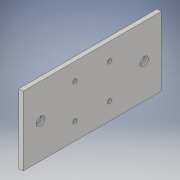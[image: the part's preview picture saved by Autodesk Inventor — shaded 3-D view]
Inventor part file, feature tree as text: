
AUTODESK INVENTOR PART (.ipt)
format: ipt  version: 2017 (Build 210142000, 142)  size: 106,496 bytes
history: native  units: in
note: dims shown in document units (in); Inventor stores cm internally (conversion verified against a paired STEP export)
features: extrude x1, sketch x1
ambient origin geometry x8: Origin, YZ Plane, XZ Plane, XY Plane, X Axis, Y Axis, Z Axis, Center Point
bodies: Solid1 (feature_tree)
feature tree (2):
  extrude  "Extrusion1"  Depth=4.0in
  sketch  "Sketch1"  dims[d11=2.0in d12=4.0in d13=0.5in d14=0.25in d15=1.0in d16=0.5in d17=0.125in d18=0.5in d19=0.125in d20=0.125in d21=0.0in]
